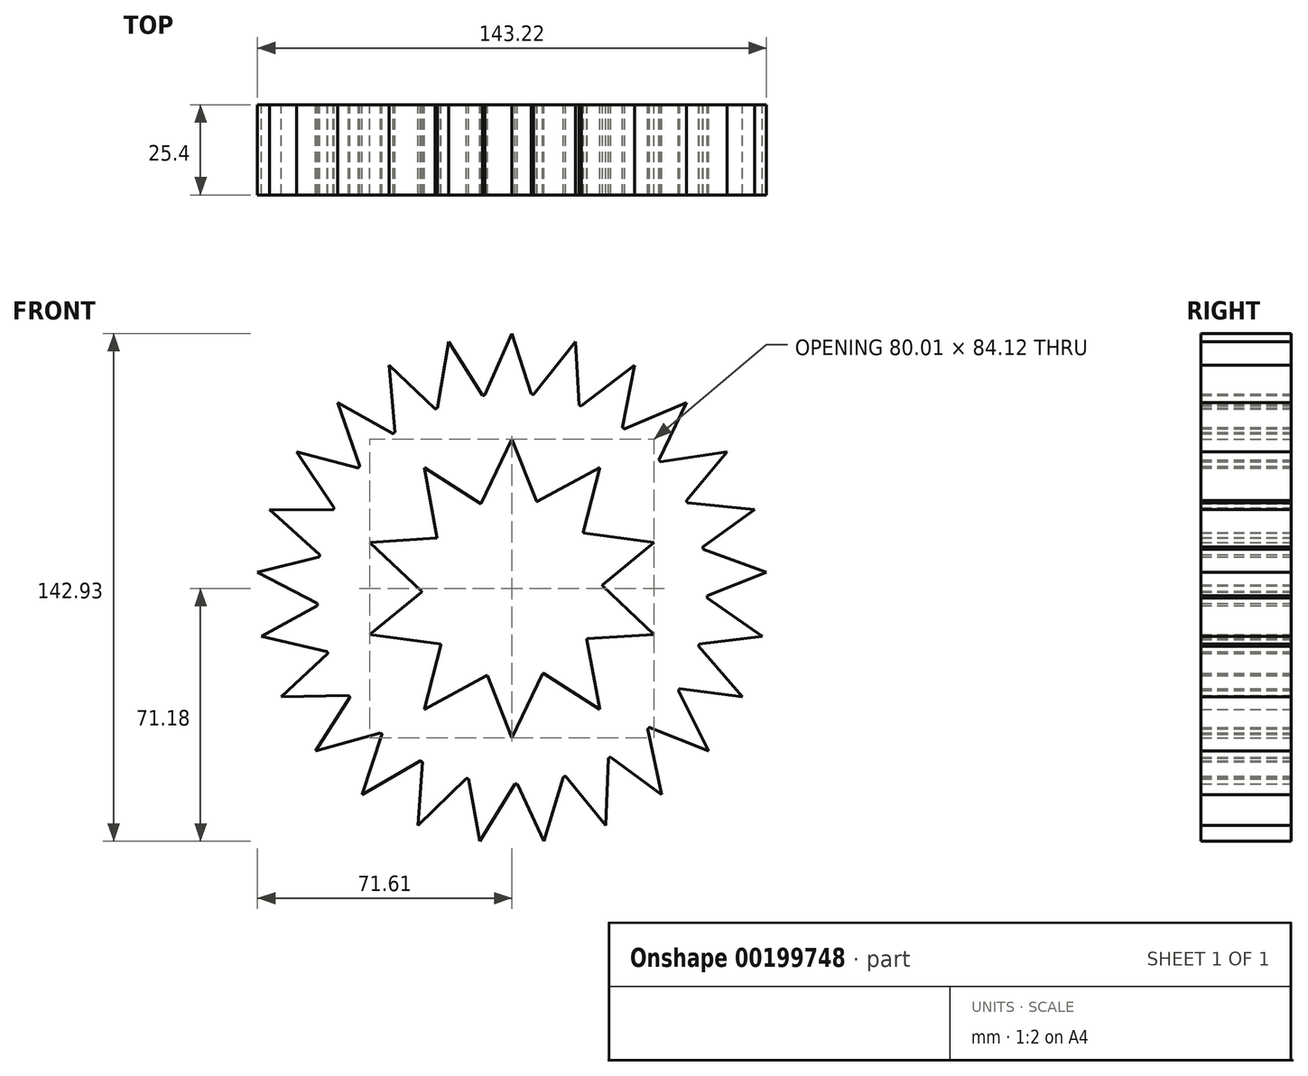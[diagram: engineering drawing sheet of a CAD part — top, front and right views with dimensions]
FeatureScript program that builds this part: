
annotation { "Feature Type Name" : "Feature", "Feature Type Description" : "" }
export const myFeature = defineFeature(function(context is Context, id is Id, definition is map)
    precondition{}
    {
        {
            var Q0;
            Q0=qCreatedBy(makeId("Front.planeOp"),FACE);
            var sketch = newSketch(context, id + "F0", { "sketchPlane" : qUnion([Q0])});
            skCircle(sketch, "E0", {"center": v(0, 0) * mm, "radius": 25.49 * mm});
            skLineSegment(sketch, "E1", {"start": v(-8.64, 23.98) * mm, "end": v(0, 42.06) * mm});
            skLineSegment(sketch, "E2", {"start": v(0, 42.06) * mm, "end": v(6.92, 24.53) * mm});
            skLineSegment(sketch, "E3.1.0", {"start": v(-24.72, 34.03) * mm, "end": v(-8.82, 23.91) * mm});
            skLineSegment(sketch, "E3.1.1", {"start": v(-21.08, 14.32) * mm, "end": v(-24.72, 34.03) * mm});
            skLineSegment(sketch, "E3.2.0", {"start": v(-40, 13) * mm, "end": v(-21.2, 14.16) * mm});
            skLineSegment(sketch, "E3.2.1", {"start": v(-25.48, -0.8) * mm, "end": v(-40, 13) * mm});
            skLineSegment(sketch, "E3.3.0", {"start": v(-40, -13) * mm, "end": v(-25.47, -1) * mm});
            skLineSegment(sketch, "E3.3.1", {"start": v(-20.14, -15.63) * mm, "end": v(-40, -13) * mm});
            skLineSegment(sketch, "E3.4.0", {"start": v(-24.72, -34.03) * mm, "end": v(-20.02, -15.78) * mm});
            skLineSegment(sketch, "E3.4.1", {"start": v(-7.1, -24.48) * mm, "end": v(-24.72, -34.03) * mm});
            skLineSegment(sketch, "E3.5.0", {"start": v(0, -42.06) * mm, "end": v(-6.92, -24.53) * mm});
            skLineSegment(sketch, "E3.5.1", {"start": v(8.64, -23.98) * mm, "end": v(0, -42.06) * mm});
            skLineSegment(sketch, "E3.6.0", {"start": v(24.72, -34.03) * mm, "end": v(8.82, -23.91) * mm});
            skLineSegment(sketch, "E3.6.1", {"start": v(21.08, -14.32) * mm, "end": v(24.72, -34.03) * mm});
            skLineSegment(sketch, "E3.7.0", {"start": v(40, -13) * mm, "end": v(21.2, -14.16) * mm});
            skLineSegment(sketch, "E3.7.1", {"start": v(25.48, 0.8) * mm, "end": v(40, -13) * mm});
            skLineSegment(sketch, "E3.8.0", {"start": v(40, 13) * mm, "end": v(25.47, 1) * mm});
            skLineSegment(sketch, "E3.8.1", {"start": v(20.14, 15.63) * mm, "end": v(40, 13) * mm});
            skLineSegment(sketch, "E3.9.0", {"start": v(24.72, 34.03) * mm, "end": v(20.02, 15.78) * mm});
            skLineSegment(sketch, "E3.9.1", {"start": v(7.1, 24.48) * mm, "end": v(24.72, 34.03) * mm});
            skCircle(sketch, "E4", {"center": v(0, 0) * mm, "radius": 54.96 * mm});
            skLineSegment(sketch, "E5", {"start": v(-7.68, 54.43) * mm, "end": v(0, 71.75) * mm});
            skLineSegment(sketch, "E6", {"start": v(0, 71.75) * mm, "end": v(5.46, 54.7) * mm});
            skPoint(sketch, "E7", {"position": v(-8.26, 6.2) * mm});
            skPoint(sketch, "E8", {"position": v(-6.33, 7.3) * mm});
            skLineSegment(sketch, "E9.1.0", {"start": v(-17.84, 69.5) * mm, "end": v(-8.31, 54.33) * mm});
            skLineSegment(sketch, "E9.1.1", {"start": v(-20.97, 50.8) * mm, "end": v(-17.84, 69.5) * mm});
            skLineSegment(sketch, "E9.2.0", {"start": v(-34.56, 62.87) * mm, "end": v(-21.56, 50.56) * mm});
            skLineSegment(sketch, "E9.2.1", {"start": v(-32.95, 44) * mm, "end": v(-34.56, 62.87) * mm});
            skLineSegment(sketch, "E9.3.0", {"start": v(-49.11, 52.3) * mm, "end": v(-33.46, 43.6) * mm});
            skLineSegment(sketch, "E9.3.1", {"start": v(-42.86, 34.42) * mm, "end": v(-49.11, 52.3) * mm});
            skLineSegment(sketch, "E9.4.0", {"start": v(-60.58, 38.44) * mm, "end": v(-43.25, 33.92) * mm});
            skLineSegment(sketch, "E9.4.1", {"start": v(-50.07, 22.68) * mm, "end": v(-60.58, 38.44) * mm});
            skLineSegment(sketch, "E9.5.0", {"start": v(-68.24, 22.17) * mm, "end": v(-50.33, 22.1) * mm});
            skLineSegment(sketch, "E9.5.1", {"start": v(-54.13, 9.51) * mm, "end": v(-68.24, 22.17) * mm});
            skLineSegment(sketch, "E9.6.0", {"start": v(-71.6, 4.5) * mm, "end": v(-54.24, 8.88) * mm});
            skLineSegment(sketch, "E9.6.1", {"start": v(-54.8, -4.25) * mm, "end": v(-71.6, 4.5) * mm});
            skLineSegment(sketch, "E9.7.0", {"start": v(-70.48, -13.44) * mm, "end": v(-54.75, -4.89) * mm});
            skLineSegment(sketch, "E9.7.1", {"start": v(-52.02, -17.74) * mm, "end": v(-70.48, -13.44) * mm});
            skLineSegment(sketch, "E9.8.0", {"start": v(-64.92, -30.55) * mm, "end": v(-51.81, -18.35) * mm});
            skLineSegment(sketch, "E9.8.1", {"start": v(-45.98, -30.12) * mm, "end": v(-64.92, -30.55) * mm});
            skLineSegment(sketch, "E9.9.0", {"start": v(-55.28, -45.73) * mm, "end": v(-45.62, -30.66) * mm});
            skLineSegment(sketch, "E9.9.1", {"start": v(-37.04, -40.6) * mm, "end": v(-55.28, -45.73) * mm});
            skLineSegment(sketch, "E9.10.0", {"start": v(-42.17, -58.04) * mm, "end": v(-36.56, -41.04) * mm});
            skLineSegment(sketch, "E9.10.1", {"start": v(-25.78, -48.55) * mm, "end": v(-42.17, -58.04) * mm});
            skLineSegment(sketch, "E9.11.0", {"start": v(-26.41, -66.7) * mm, "end": v(-25.2, -48.84) * mm});
            skLineSegment(sketch, "E9.11.1", {"start": v(-12.9, -53.43) * mm, "end": v(-26.41, -66.7) * mm});
            skLineSegment(sketch, "E9.12.0", {"start": v(-9, -71.18) * mm, "end": v(-12.27, -53.58) * mm});
            skLineSegment(sketch, "E9.12.1", {"start": v(0.8, -54.96) * mm, "end": v(-9, -71.18) * mm});
            skLineSegment(sketch, "E9.13.0", {"start": v(9, -71.18) * mm, "end": v(1.44, -54.95) * mm});
            skLineSegment(sketch, "E9.13.1", {"start": v(14.44, -53.03) * mm, "end": v(9, -71.18) * mm});
            skLineSegment(sketch, "E9.14.0", {"start": v(26.41, -66.7) * mm, "end": v(15.06, -52.86) * mm});
            skLineSegment(sketch, "E9.14.1", {"start": v(27.18, -47.78) * mm, "end": v(26.41, -66.7) * mm});
            skLineSegment(sketch, "E9.15.0", {"start": v(42.17, -58.04) * mm, "end": v(27.73, -47.46) * mm});
            skLineSegment(sketch, "E9.15.1", {"start": v(38.2, -39.52) * mm, "end": v(42.17, -58.04) * mm});
            skLineSegment(sketch, "E9.16.0", {"start": v(55.28, -45.73) * mm, "end": v(38.66, -39.07) * mm});
            skLineSegment(sketch, "E9.16.1", {"start": v(46.83, -28.77) * mm, "end": v(55.28, -45.73) * mm});
            skLineSegment(sketch, "E9.17.0", {"start": v(64.92, -30.55) * mm, "end": v(47.16, -28.23) * mm});
            skLineSegment(sketch, "E9.17.1", {"start": v(52.52, -16.22) * mm, "end": v(64.92, -30.55) * mm});
            skLineSegment(sketch, "E9.18.0", {"start": v(70.48, -13.44) * mm, "end": v(52.7, -15.61) * mm});
            skLineSegment(sketch, "E9.18.1", {"start": v(54.9, -2.65) * mm, "end": v(70.48, -13.44) * mm});
            skLineSegment(sketch, "E9.19.0", {"start": v(71.6, 4.5) * mm, "end": v(54.93, -2.01) * mm});
            skLineSegment(sketch, "E9.19.1", {"start": v(53.84, 11.08) * mm, "end": v(71.6, 4.5) * mm});
            skLineSegment(sketch, "E9.20.0", {"start": v(68.24, 22.17) * mm, "end": v(53.7, 11.7) * mm});
            skLineSegment(sketch, "E9.20.1", {"start": v(49.39, 24.12) * mm, "end": v(68.24, 22.17) * mm});
            skLineSegment(sketch, "E9.21.0", {"start": v(60.58, 38.44) * mm, "end": v(49.1, 24.7) * mm});
            skLineSegment(sketch, "E9.21.1", {"start": v(41.84, 35.65) * mm, "end": v(60.58, 38.44) * mm});
            skLineSegment(sketch, "E9.22.0", {"start": v(49.11, 52.3) * mm, "end": v(41.42, 36.13) * mm});
            skLineSegment(sketch, "E9.22.1", {"start": v(31.66, 44.93) * mm, "end": v(49.11, 52.3) * mm});
            skLineSegment(sketch, "E9.23.0", {"start": v(34.56, 62.87) * mm, "end": v(31.13, 45.3) * mm});
            skLineSegment(sketch, "E9.23.1", {"start": v(19.49, 51.4) * mm, "end": v(34.56, 62.87) * mm});
            skLineSegment(sketch, "E9.24.0", {"start": v(17.84, 69.5) * mm, "end": v(18.89, 51.62) * mm});
            skLineSegment(sketch, "E9.24.1", {"start": v(6.1, 54.63) * mm, "end": v(17.84, 69.5) * mm});
            skCircle(sketch, "E10", {"center": v(-8.26, 6.2) * mm, "radius": 1.87 * mm});
            skCircle(sketch, "E11", {"center": v(-2.36, 0) * mm, "radius": 1.53 * mm});
            skCircle(sketch, "E12", {"center": v(2.82, 6.19) * mm, "radius": 2.24 * mm});
            skSolve(sketch);
        }
        {
            var Q0;
            {var subQ45=sQuery(id+"F0.wireOp",EDGE,"E1");Q0=makeQuery(id+"F0.imprint","IMPRINT",FACE,{"disambiguationData":[TD([[makeQuery(id+"F0.imprint","IMPRINT",EDGE,{"derivedFrom":subQ45}),1.0]])]});}
            var Q1;
            {var subQ0=sQuery(id+"F0.wireOp",EDGE,"E9.3.0");Q1=makeQuery(id+"F0.imprint","IMPRINT",FACE,{"disambiguationData":[TD([[makeQuery(id+"F0.imprint","IMPRINT",EDGE,{"derivedFrom":subQ0}),-1.0]])]});}
            var Q2;
            {var subQ0=sQuery(id+"F0.wireOp",EDGE,"E9.4.0");Q2=makeQuery(id+"F0.imprint","IMPRINT",FACE,{"disambiguationData":[TD([[makeQuery(id+"F0.imprint","IMPRINT",EDGE,{"derivedFrom":subQ0}),-1.0]])]});}
            var Q3;
            {var subQ0=sQuery(id+"F0.wireOp",EDGE,"E9.5.0");Q3=makeQuery(id+"F0.imprint","IMPRINT",FACE,{"disambiguationData":[TD([[makeQuery(id+"F0.imprint","IMPRINT",EDGE,{"derivedFrom":subQ0}),-1.0]])]});}
            var Q4;
            {var subQ0=sQuery(id+"F0.wireOp",EDGE,"E9.6.0");Q4=makeQuery(id+"F0.imprint","IMPRINT",FACE,{"disambiguationData":[TD([[makeQuery(id+"F0.imprint","IMPRINT",EDGE,{"derivedFrom":subQ0}),-1.0]])]});}
            var Q5;
            {var subQ0=sQuery(id+"F0.wireOp",EDGE,"E9.9.0");Q5=makeQuery(id+"F0.imprint","IMPRINT",FACE,{"disambiguationData":[TD([[makeQuery(id+"F0.imprint","IMPRINT",EDGE,{"derivedFrom":subQ0}),-1.0]])]});}
            var Q6;
            {var subQ0=sQuery(id+"F0.wireOp",EDGE,"E9.10.0");Q6=makeQuery(id+"F0.imprint","IMPRINT",FACE,{"disambiguationData":[TD([[makeQuery(id+"F0.imprint","IMPRINT",EDGE,{"derivedFrom":subQ0}),-1.0]])]});}
            var Q7;
            {var subQ0=sQuery(id+"F0.wireOp",EDGE,"E9.11.0");Q7=makeQuery(id+"F0.imprint","IMPRINT",FACE,{"disambiguationData":[TD([[makeQuery(id+"F0.imprint","IMPRINT",EDGE,{"derivedFrom":subQ0}),-1.0]])]});}
            var Q8;
            {var subQ0=sQuery(id+"F0.wireOp",EDGE,"E9.12.0");Q8=makeQuery(id+"F0.imprint","IMPRINT",FACE,{"disambiguationData":[TD([[makeQuery(id+"F0.imprint","IMPRINT",EDGE,{"derivedFrom":subQ0}),-1.0]])]});}
            var Q9;
            {var subQ0=sQuery(id+"F0.wireOp",EDGE,"E9.13.0");Q9=makeQuery(id+"F0.imprint","IMPRINT",FACE,{"disambiguationData":[TD([[makeQuery(id+"F0.imprint","IMPRINT",EDGE,{"derivedFrom":subQ0}),-1.0]])]});}
            var Q10;
            {var subQ0=sQuery(id+"F0.wireOp",EDGE,"E9.14.0");Q10=makeQuery(id+"F0.imprint","IMPRINT",FACE,{"disambiguationData":[TD([[makeQuery(id+"F0.imprint","IMPRINT",EDGE,{"derivedFrom":subQ0}),-1.0]])]});}
            var Q11;
            {var subQ0=sQuery(id+"F0.wireOp",EDGE,"E9.15.0");Q11=makeQuery(id+"F0.imprint","IMPRINT",FACE,{"disambiguationData":[TD([[makeQuery(id+"F0.imprint","IMPRINT",EDGE,{"derivedFrom":subQ0}),-1.0]])]});}
            var Q12;
            {var subQ0=sQuery(id+"F0.wireOp",EDGE,"E9.16.0");Q12=makeQuery(id+"F0.imprint","IMPRINT",FACE,{"disambiguationData":[TD([[makeQuery(id+"F0.imprint","IMPRINT",EDGE,{"derivedFrom":subQ0}),-1.0]])]});}
            var Q13;
            {var subQ0=sQuery(id+"F0.wireOp",EDGE,"E9.17.0");Q13=makeQuery(id+"F0.imprint","IMPRINT",FACE,{"disambiguationData":[TD([[makeQuery(id+"F0.imprint","IMPRINT",EDGE,{"derivedFrom":subQ0}),-1.0]])]});}
            var Q14;
            {var subQ0=sQuery(id+"F0.wireOp",EDGE,"E9.18.0");Q14=makeQuery(id+"F0.imprint","IMPRINT",FACE,{"disambiguationData":[TD([[makeQuery(id+"F0.imprint","IMPRINT",EDGE,{"derivedFrom":subQ0}),-1.0]])]});}
            var Q15;
            {var subQ0=sQuery(id+"F0.wireOp",EDGE,"E9.19.0");Q15=makeQuery(id+"F0.imprint","IMPRINT",FACE,{"disambiguationData":[TD([[makeQuery(id+"F0.imprint","IMPRINT",EDGE,{"derivedFrom":subQ0}),-1.0]])]});}
            var Q16;
            {var subQ0=sQuery(id+"F0.wireOp",EDGE,"E9.20.0");Q16=makeQuery(id+"F0.imprint","IMPRINT",FACE,{"disambiguationData":[TD([[makeQuery(id+"F0.imprint","IMPRINT",EDGE,{"derivedFrom":subQ0}),-1.0]])]});}
            var Q17;
            {var subQ0=sQuery(id+"F0.wireOp",EDGE,"E9.21.0");Q17=makeQuery(id+"F0.imprint","IMPRINT",FACE,{"disambiguationData":[TD([[makeQuery(id+"F0.imprint","IMPRINT",EDGE,{"derivedFrom":subQ0}),-1.0]])]});}
            var Q18;
            {var subQ0=sQuery(id+"F0.wireOp",EDGE,"E9.22.0");Q18=makeQuery(id+"F0.imprint","IMPRINT",FACE,{"disambiguationData":[TD([[makeQuery(id+"F0.imprint","IMPRINT",EDGE,{"derivedFrom":subQ0}),-1.0]])]});}
            var Q19;
            {var subQ0=sQuery(id+"F0.wireOp",EDGE,"E9.23.0");Q19=makeQuery(id+"F0.imprint","IMPRINT",FACE,{"disambiguationData":[TD([[makeQuery(id+"F0.imprint","IMPRINT",EDGE,{"derivedFrom":subQ0}),-1.0]])]});}
            var Q20;
            {var subQ0=sQuery(id+"F0.wireOp",EDGE,"E9.24.0");Q20=makeQuery(id+"F0.imprint","IMPRINT",FACE,{"disambiguationData":[TD([[makeQuery(id+"F0.imprint","IMPRINT",EDGE,{"derivedFrom":subQ0}),-1.0]])]});}
            var Q21;
            {var subQ0=sQuery(id+"F0.wireOp",EDGE,"E5");Q21=makeQuery(id+"F0.imprint","IMPRINT",FACE,{"disambiguationData":[TD([[makeQuery(id+"F0.imprint","IMPRINT",EDGE,{"derivedFrom":subQ0}),-1.0]])]});}
            var Q22;
            {var subQ0=sQuery(id+"F0.wireOp",EDGE,"E9.1.0");Q22=makeQuery(id+"F0.imprint","IMPRINT",FACE,{"disambiguationData":[TD([[makeQuery(id+"F0.imprint","IMPRINT",EDGE,{"derivedFrom":subQ0}),-1.0]])]});}
            var Q23;
            {var subQ0=sQuery(id+"F0.wireOp",EDGE,"E9.7.0");Q23=makeQuery(id+"F0.imprint","IMPRINT",FACE,{"disambiguationData":[TD([[makeQuery(id+"F0.imprint","IMPRINT",EDGE,{"derivedFrom":subQ0}),-1.0]])]});}
            var Q24;
            {var subQ0=sQuery(id+"F0.wireOp",EDGE,"E9.8.0");Q24=makeQuery(id+"F0.imprint","IMPRINT",FACE,{"disambiguationData":[TD([[makeQuery(id+"F0.imprint","IMPRINT",EDGE,{"derivedFrom":subQ0}),-1.0]])]});}
            var Q25;
            {var subQ0=sQuery(id+"F0.wireOp",EDGE,"E9.2.0");Q25=makeQuery(id+"F0.imprint","IMPRINT",FACE,{"disambiguationData":[TD([[makeQuery(id+"F0.imprint","IMPRINT",EDGE,{"derivedFrom":subQ0}),-1.0]])]});}
            extrude(context, id + "F1", {"entities" : qUnion([Q0, Q1, Q2, Q3, Q4, Q5, Q6, Q7, Q8, Q9, Q10, Q11, Q12, Q13, Q14, Q15, Q16, Q17, Q18, Q19, Q20, Q21, Q22, Q23, Q24, Q25]), "depth" : 25.4 * mm});
        }
    });
